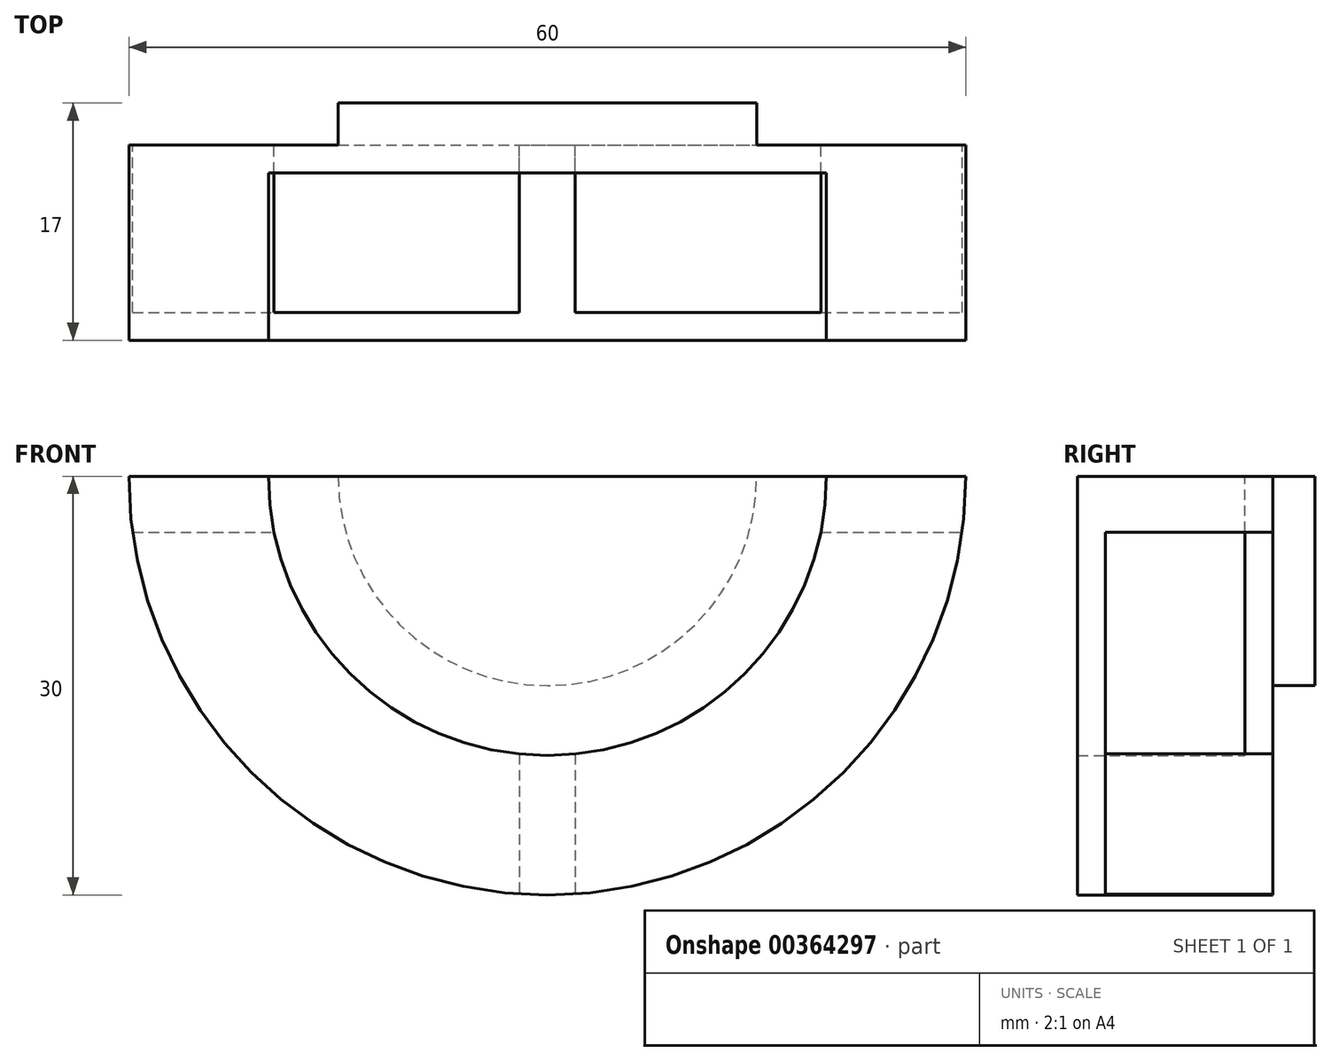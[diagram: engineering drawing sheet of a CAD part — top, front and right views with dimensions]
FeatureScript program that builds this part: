
annotation { "Feature Type Name" : "Feature", "Feature Type Description" : "" }
export const myFeature = defineFeature(function(context is Context, id is Id, definition is map)
    precondition{}
    {
        {
            var Q0;
            Q0=qCreatedBy(makeId("Front.planeOp"),FACE);
            var sketch = newSketch(context, id + "F0", { "sketchPlane" : qUnion([Q0])});
            skArc(sketch, "E0", {"start": v(-15, 0) * mm, "mid": v(0, -15) * mm, "end": v(15, 0) * mm});
            skLineSegment(sketch, "E1", {"start": v(-15, 0) * mm, "end": v(15, 0) * mm});
            skSolve(sketch);
        }
        {
            var Q0;
            Q0 = qSketchRegion(id + "F0", true);
            extrude(context, id + "F1", {"entities" : qUnion([Q0]), "oppositeDirection" : true, "depth" : 3 * mm, "offsetDistance" : 25 * mm});
        }
        {
            var Q0;
            Q0=makeQuery(id+"F1.opExtrude","CAP_FACE",FACE,{"disambiguationData":[OSD([sQuery(id+"F0.wireOp",EDGE,"E0"),sQuery(id+"F0.wireOp",EDGE,"E1")])],"isStart":true});
            var sketch = newSketch(context, id + "F2", { "sketchPlane" : qUnion([Q0])});
            skArc(sketch, "E2", {"start": v(-20, 0) * mm, "mid": v(0, -20) * mm, "end": v(20, 0) * mm});
            skLineSegment(sketch, "E3", {"start": v(-20, 0) * mm, "end": v(20, 0) * mm});
            skArc(sketch, "E4", {"start": v(30, 0) * mm, "mid": v(0, -30) * mm, "end": v(-30, 0) * mm});
            skLineSegment(sketch, "E5", {"start": v(-20, 0) * mm, "end": v(-30, 0) * mm});
            skLineSegment(sketch, "E6", {"start": v(20, 0) * mm, "end": v(30, 0) * mm});
            skLineSegment(sketch, "E7", {"start": v(-29.73, -4) * mm, "end": v(29.73, -4) * mm});
            skLineSegment(sketch, "E8", {"start": v(0, 0) * mm, "end": v(0, -30) * mm, "construction": true});
            skLineSegment(sketch, "E9", {"start": v(-2, -19.9) * mm, "end": v(-2, -29.93) * mm});
            skLineSegment(sketch, "E10.MirrorCS", {"start": v(2, -19.9) * mm, "end": v(2, -29.93) * mm});
            skSolve(sketch);
        }
        {
            var Q0;
            {var subQ0=sQuery(id+"F2.wireOp",EDGE,"E2");var subQ4=makeQuery(id+"F2.imprint","INTERSECT",VERTEX,{"derivedFrom":[subQ0,sQuery(id+"F2.wireOp",EDGE,"E9")]});Q0=makeQuery(id+"F2.imprint","IMPRINT",FACE,{"disambiguationData":[TD([[makeQuery(id+"F2.imprint","IMPRINT",EDGE,{"disambiguationData":[TD([[subQ4,1.0]])],"derivedFrom":subQ0}),1.0]])]});}
            var Q1;
            {var subQ0=sQuery(id+"F2.wireOp",EDGE,"E7");var subQ1=makeQuery(id+"F1.opExtrude","CAP_EDGE",EDGE,{"disambiguationData":[OSD([sQuery(id+"F0.wireOp",EDGE,"E0")])],"isStart":true});var subQ2=makeQuery(id+"F2.imprint","INTERSECT",VERTEX,{"disambiguationData":[OD(0.0)],"derivedFrom":[subQ1,subQ0]});Q1=makeQuery(id+"F2.imprint","IMPRINT",FACE,{"disambiguationData":[TD([[makeQuery(id+"F2.imprint","IMPRINT",EDGE,{"disambiguationData":[TD([[subQ2,-1.0]])],"derivedFrom":subQ0}),-1.0]])]});}
            var Q2;
            {var subQ1=sQuery(id+"F2.wireOp",EDGE,"E2");var subQ3=sQuery(id+"F2.wireOp",EDGE,"E7");var subQ4=makeQuery(id+"F2.imprint","INTERSECT",VERTEX,{"disambiguationData":[OD(0.0)],"derivedFrom":[subQ1,subQ3]});Q2=makeQuery(id+"F2.imprint","IMPRINT",FACE,{"disambiguationData":[TD([[makeQuery(id+"F2.imprint","IMPRINT",EDGE,{"disambiguationData":[TD([[subQ4,-1.0]])],"derivedFrom":subQ3}),1.0]])]});}
            var Q3;
            {var subQ1=sQuery(id+"F2.wireOp",EDGE,"E2");var subQ3=sQuery(id+"F2.wireOp",EDGE,"E7");var subQ4=makeQuery(id+"F2.imprint","INTERSECT",VERTEX,{"disambiguationData":[OD(1.0)],"derivedFrom":[subQ1,subQ3]});Q3=makeQuery(id+"F2.imprint","IMPRINT",FACE,{"disambiguationData":[TD([[makeQuery(id+"F2.imprint","IMPRINT",EDGE,{"disambiguationData":[TD([[subQ4,1.0]])],"derivedFrom":subQ3}),1.0]])]});}
            var Q4;
            {var subQ0=sQuery(id+"F2.wireOp",EDGE,"E3");var subQ1=makeQuery(id+"F1.opExtrude","CAP_EDGE",EDGE,{"disambiguationData":[OSD([sQuery(id+"F0.wireOp",EDGE,"E0")])],"isStart":true});var subQ2=makeQuery(id+"F2.imprint","INTERSECT",VERTEX,{"disambiguationData":[OD(0.0)],"derivedFrom":[subQ1,subQ0]});Q4=makeQuery(id+"F2.imprint","IMPRINT",FACE,{"disambiguationData":[TD([[makeQuery(id+"F2.imprint","IMPRINT",EDGE,{"disambiguationData":[TD([[subQ2,-1.0]])],"derivedFrom":subQ0}),-1.0]])]});}
            var Q5;
            {var subQ0=sQuery(id+"F2.wireOp",EDGE,"E5");Q5=makeQuery(id+"F2.imprint","IMPRINT",FACE,{"disambiguationData":[TD([[makeQuery(id+"F2.imprint","IMPRINT",EDGE,{"derivedFrom":subQ0}),1.0]])]});}
            var Q6;
            {var subQ0=sQuery(id+"F2.wireOp",EDGE,"E6");Q6=makeQuery(id+"F2.imprint","IMPRINT",FACE,{"disambiguationData":[TD([[makeQuery(id+"F2.imprint","IMPRINT",EDGE,{"derivedFrom":subQ0}),-1.0]])]});}
            var Q7;
            {var subQ0=sQuery(id+"F2.wireOp",EDGE,"E9");Q7=makeQuery(id+"F2.imprint","IMPRINT",FACE,{"disambiguationData":[TD([[makeQuery(id+"F2.imprint","IMPRINT",EDGE,{"derivedFrom":subQ0}),1.0]])]});}
            extrude(context, id + "F3", {"entities" : qUnion([Q0, Q1, Q2, Q3, Q4, Q5, Q6, Q7]), "operationType" : NewBodyOperationType.ADD, "depth" : 2 * mm, "offsetDistance" : 25 * mm});
        }
        {
            var Q0;
            {var subQ0=sQuery(id+"F2.wireOp",EDGE,"E5");Q0=makeQuery(id+"F2.imprint","IMPRINT",FACE,{"disambiguationData":[TD([[makeQuery(id+"F2.imprint","IMPRINT",EDGE,{"derivedFrom":subQ0}),1.0]])]});}
            var Q1;
            {var subQ0=sQuery(id+"F2.wireOp",EDGE,"E6");Q1=makeQuery(id+"F2.imprint","IMPRINT",FACE,{"disambiguationData":[TD([[makeQuery(id+"F2.imprint","IMPRINT",EDGE,{"derivedFrom":subQ0}),-1.0]])]});}
            var Q2;
            {var subQ0=sQuery(id+"F2.wireOp",EDGE,"E9");Q2=makeQuery(id+"F2.imprint","IMPRINT",FACE,{"disambiguationData":[TD([[makeQuery(id+"F2.imprint","IMPRINT",EDGE,{"derivedFrom":subQ0}),1.0]])]});}
            extrude(context, id + "F4", {"entities" : qUnion([Q0, Q1, Q2]), "operationType" : NewBodyOperationType.ADD, "depth" : 12 * mm, "offsetDistance" : 25 * mm});
        }
        {
            var Q0;
            {var subQ0=sQuery(id+"F2.wireOp",EDGE,"E9");Q0=makeQuery(id+"F2.imprint","IMPRINT",FACE,{"disambiguationData":[TD([[makeQuery(id+"F2.imprint","IMPRINT",EDGE,{"derivedFrom":subQ0}),-1.0]])]});}
            var Q1;
            {var subQ0=sQuery(id+"F2.wireOp",EDGE,"E10.MirrorCS");Q1=makeQuery(id+"F2.imprint","IMPRINT",FACE,{"disambiguationData":[TD([[makeQuery(id+"F2.imprint","IMPRINT",EDGE,{"derivedFrom":subQ0}),1.0]])]});}
            var Q2;
            {var subQ0=sQuery(id+"F2.wireOp",EDGE,"E5");Q2=makeQuery(id+"F2.imprint","IMPRINT",FACE,{"disambiguationData":[TD([[makeQuery(id+"F2.imprint","IMPRINT",EDGE,{"derivedFrom":subQ0}),1.0]])]});}
            var Q3;
            {var subQ0=sQuery(id+"F2.wireOp",EDGE,"E9");Q3=makeQuery(id+"F2.imprint","IMPRINT",FACE,{"disambiguationData":[TD([[makeQuery(id+"F2.imprint","IMPRINT",EDGE,{"derivedFrom":subQ0}),1.0]])]});}
            var Q4;
            {var subQ0=sQuery(id+"F2.wireOp",EDGE,"E6");Q4=makeQuery(id+"F2.imprint","IMPRINT",FACE,{"disambiguationData":[TD([[makeQuery(id+"F2.imprint","IMPRINT",EDGE,{"derivedFrom":subQ0}),-1.0]])]});}
            var Q5;
            Q5=makeQuery(id+"F4.opExtrude","CAP_FACE",FACE,{"disambiguationData":[OSD([sQuery(id+"F2.wireOp",EDGE,"E2"),sQuery(id+"F2.wireOp",EDGE,"E4"),sQuery(id+"F2.wireOp",EDGE,"E9"),sQuery(id+"F2.wireOp",EDGE,"E10.MirrorCS")])],"isStart":false});
            var Q6;
            Q6=makeQuery(id+"F4.opExtrude","CAP_FACE",FACE,{"disambiguationData":[OSD([sQuery(id+"F2.wireOp",EDGE,"E2"),sQuery(id+"F2.wireOp",EDGE,"E4"),sQuery(id+"F2.wireOp",EDGE,"E9"),sQuery(id+"F2.wireOp",EDGE,"E10.MirrorCS")])],"isStart":false});
            extrude(context, id + "F5", {"entities" : qUnion([Q0, Q1, Q2, Q3, Q4]), "operationType" : NewBodyOperationType.ADD, "endBound" : BoundingType.UP_TO_SURFACE, "depth" : 25 * mm, "endBoundEntityFace" : qUnion([Q5]), "hasOffset" : true, "offsetDistance" : 2 * mm, "offsetOppositeDirection" : true, "hasSecondDirection" : true, "secondDirectionBound" : BoundingType.UP_TO_SURFACE, "secondDirectionOppositeDirection" : false, "secondDirectionDepth" : 25 * mm, "secondDirectionBoundEntityFace" : qUnion([Q6])});
        }
    });
